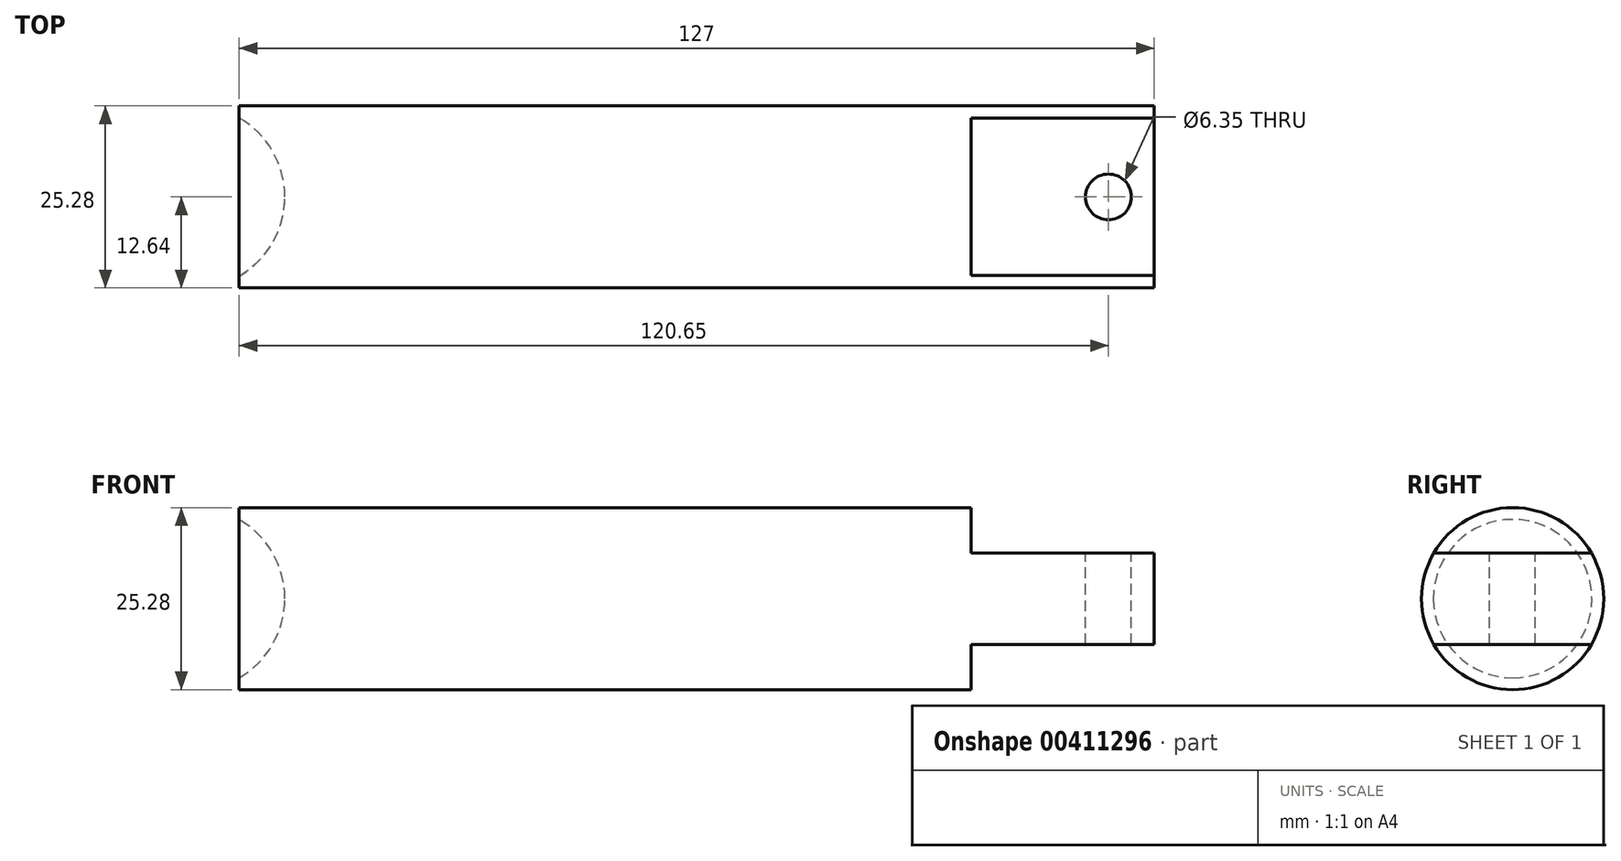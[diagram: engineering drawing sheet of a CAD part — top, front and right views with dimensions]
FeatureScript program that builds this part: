
annotation { "Feature Type Name" : "Feature", "Feature Type Description" : "" }
export const myFeature = defineFeature(function(context is Context, id is Id, definition is map)
    precondition{}
    {
        {
            var Q0;
            Q0=qCreatedBy(makeId("Right.planeOp"),FACE);
            var sketch = newSketch(context, id + "F0", { "sketchPlane" : qUnion([Q0])});
            skCircle(sketch, "E0", {"center": v(0, 0) * mm, "radius": 12.64 * mm});
            skSolve(sketch);
        }
        {
            var Q0;
            Q0 = qSketchRegion(id + "F0", true);
            extrude(context, id + "F1", {"entities" : qUnion([Q0]), "endBound" : BoundingType.SYMMETRIC, "depth" : 127 * mm});
        }
        {
            var Q0;
            Q0=qCreatedBy(makeId("Front.planeOp"),FACE);
            var sketch = newSketch(context, id + "F2", { "sketchPlane" : qUnion([Q0])});
            skLineSegment(sketch, "E1", {"start": v(38.1, 12.7) * mm, "end": v(38.1, 6.35) * mm});
            skLineSegment(sketch, "E2", {"start": v(38.1, 6.35) * mm, "end": v(63.5, 6.35) * mm});
            skLineSegment(sketch, "E3", {"start": v(63.5, 6.35) * mm, "end": v(63.5, -6.35) * mm});
            skLineSegment(sketch, "E4", {"start": v(63.5, -6.35) * mm, "end": v(38.1, -6.35) * mm});
            skLineSegment(sketch, "E5", {"start": v(38.1, -6.35) * mm, "end": v(38.1, -12.7) * mm});
            skLineSegment(sketch, "E6", {"start": v(38.1, -12.7) * mm, "end": v(68.58, -12.7) * mm});
            skLineSegment(sketch, "E7", {"start": v(68.58, -12.7) * mm, "end": v(68.58, 12.7) * mm});
            skLineSegment(sketch, "E8", {"start": v(68.58, 12.7) * mm, "end": v(38.1, 12.7) * mm});
            skSolve(sketch);
        }
        {
            var Q0;
            Q0 = qSketchRegion(id + "F2", true);
            extrude(context, id + "F3", {"entities" : qUnion([Q0]), "operationType" : NewBodyOperationType.REMOVE, "endBound" : BoundingType.SYMMETRIC, "oppositeDirection" : true, "depth" : 25.4 * mm});
        }
        {
            var Q0;
            Q0=makeQuery(id+"F3.boolean.opBoolean","COPY",FACE,{"derivedFrom":makeQuery(id+"F3.opExtrude","SWEPT_FACE",FACE,{"disambiguationData":[OSD([sQuery(id+"F2.wireOp",EDGE,"E2")])]})});
            var sketch = newSketch(context, id + "F4", { "sketchPlane" : qUnion([Q0])});
            skCircle(sketch, "E9", {"center": v(57.15, 0) * mm, "radius": 3.18 * mm});
            skSolve(sketch);
        }
        {
            var Q0;
            Q0 = qSketchRegion(id + "F4", true);
            extrude(context, id + "F5", {"entities" : qUnion([Q0]), "operationType" : NewBodyOperationType.REMOVE, "endBound" : BoundingType.UP_TO_NEXT, "oppositeDirection" : true, "depth" : 25.4 * mm});
        }
        {
            var Q0;
            Q0=qCreatedBy(makeId("Top.planeOp"),FACE);
            var sketch = newSketch(context, id + "F6", { "sketchPlane" : qUnion([Q0])});
            skArc(sketch, "E10", {"start": v(-57.15, 0) * mm, "mid": v(-58.85, 6.35) * mm, "end": v(-63.5, 11) * mm});
            skLineSegment(sketch, "E11", {"start": v(0, 0) * mm, "end": v(-69.85, 0) * mm, "construction": true});
            skLineSegment(sketch, "E12", {"start": v(-63.5, 11) * mm, "end": v(-63.5, 0) * mm});
            skLineSegment(sketch, "E13", {"start": v(-63.5, 0) * mm, "end": v(-57.15, 0) * mm});
            skSolve(sketch);
        }
        {
            var Q0;
            Q0 = qSketchRegion(id + "F6", true);
            var Q1;
            Q1=sQuery(id+"F6.wireOp",EDGE,"E11");
            revolve(context, id + "F7", {"operationType" : NewBodyOperationType.REMOVE, "entities" : qUnion([Q0]), "axis" : qUnion([Q1]), "revolveType" : RevolveType.FULL});
        }
    });
